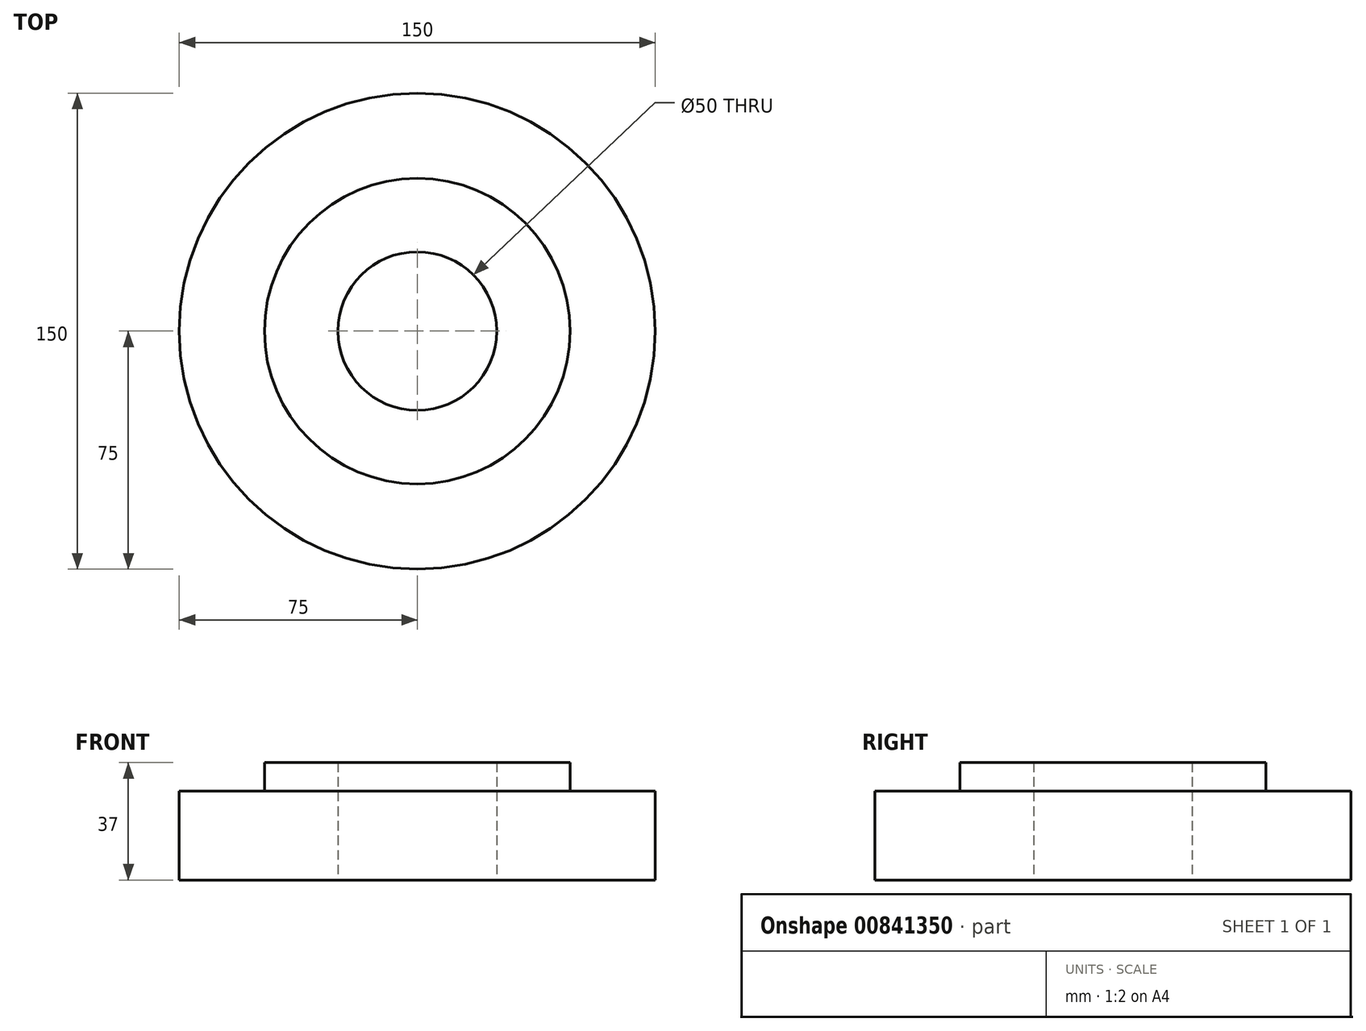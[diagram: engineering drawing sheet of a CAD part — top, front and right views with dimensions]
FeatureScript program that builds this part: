
annotation { "Feature Type Name" : "Feature", "Feature Type Description" : "" }
export const myFeature = defineFeature(function(context is Context, id is Id, definition is map)
    precondition{}
    {
        {
            var Q0;
            Q0=qCreatedBy(makeId("Top.planeOp"),FACE);
            var sketch = newSketch(context, id + "F0", { "sketchPlane" : qUnion([Q0])});
            skCircle(sketch, "E0", {"center": v(0, 0) * mm, "radius": 75 * mm});
            skCircle(sketch, "E1", {"center": v(0, 0) * mm, "radius": 25 * mm});
            skSolve(sketch);
        }
        {
            var Q0;
            Q0=qSketchRegion(id+"F0",true);
            extrude(context, id + "F1", {"entities" : qUnion([Q0]), "depth" : 28 * mm, "offsetDistance" : 25.4 * mm});
        }
        {
            var Q0;
            Q0=makeQuery(id+"F1.opExtrude","CAP_FACE",FACE,{"disambiguationData":[OSD([sQuery(id+"F0.wireOp",EDGE,"E0"),sQuery(id+"F0.wireOp",EDGE,"E1")])],"isStart":false});
            var sketch = newSketch(context, id + "F2", { "sketchPlane" : qUnion([Q0])});
            skCircle(sketch, "E2", {"center": v(0, 0) * mm, "radius": 48.15 * mm});
            skSolve(sketch);
        }
        {
            var Q0;
            Q0=makeQuery(id+"F2.imprint","IMPRINT",FACE,{"disambiguationData":[TD([[makeQuery(id+"F2.imprint","IMPRINT",EDGE,{"derivedFrom":sQuery(id+"F2.wireOp",EDGE,"E2")}),1.0]])]});
            extrude(context, id + "F3", {"entities" : qUnion([Q0]), "operationType" : NewBodyOperationType.ADD, "depth" : 9 * mm, "offsetDistance" : 25 * mm});
        }
        {
            var Q0;
            Q0=makeQuery(id+"F3.opExtrude","CAP_FACE",FACE,{"disambiguationData":[OSD([sQuery(id+"F0.wireOp",EDGE,"E1"),sQuery(id+"F2.wireOp",EDGE,"E2")])],"isStart":false});
            var sketch = newSketch(context, id + "F4", { "sketchPlane" : qUnion([Q0])});
            skCircle(sketch, "E3", {"center": v(0, 0) * mm, "radius": 39.94 * mm});
            skSolve(sketch);
        }
        {
            var Q0;
            Q0=makeQuery(id+"F4.imprint","IMPRINT",FACE,{"disambiguationData":[TD([[makeQuery(id+"F4.imprint","IMPRINT",EDGE,{"derivedFrom":sQuery(id+"F4.wireOp",EDGE,"E3")}),1.0]])]});
            extrude(context, id + "F5", {"entities" : qUnion([Q0]), "operationType" : NewBodyOperationType.ADD, "oppositeDirection" : true, "depth" : 15 * mm, "offsetDistance" : 25 * mm});
        }
    });
